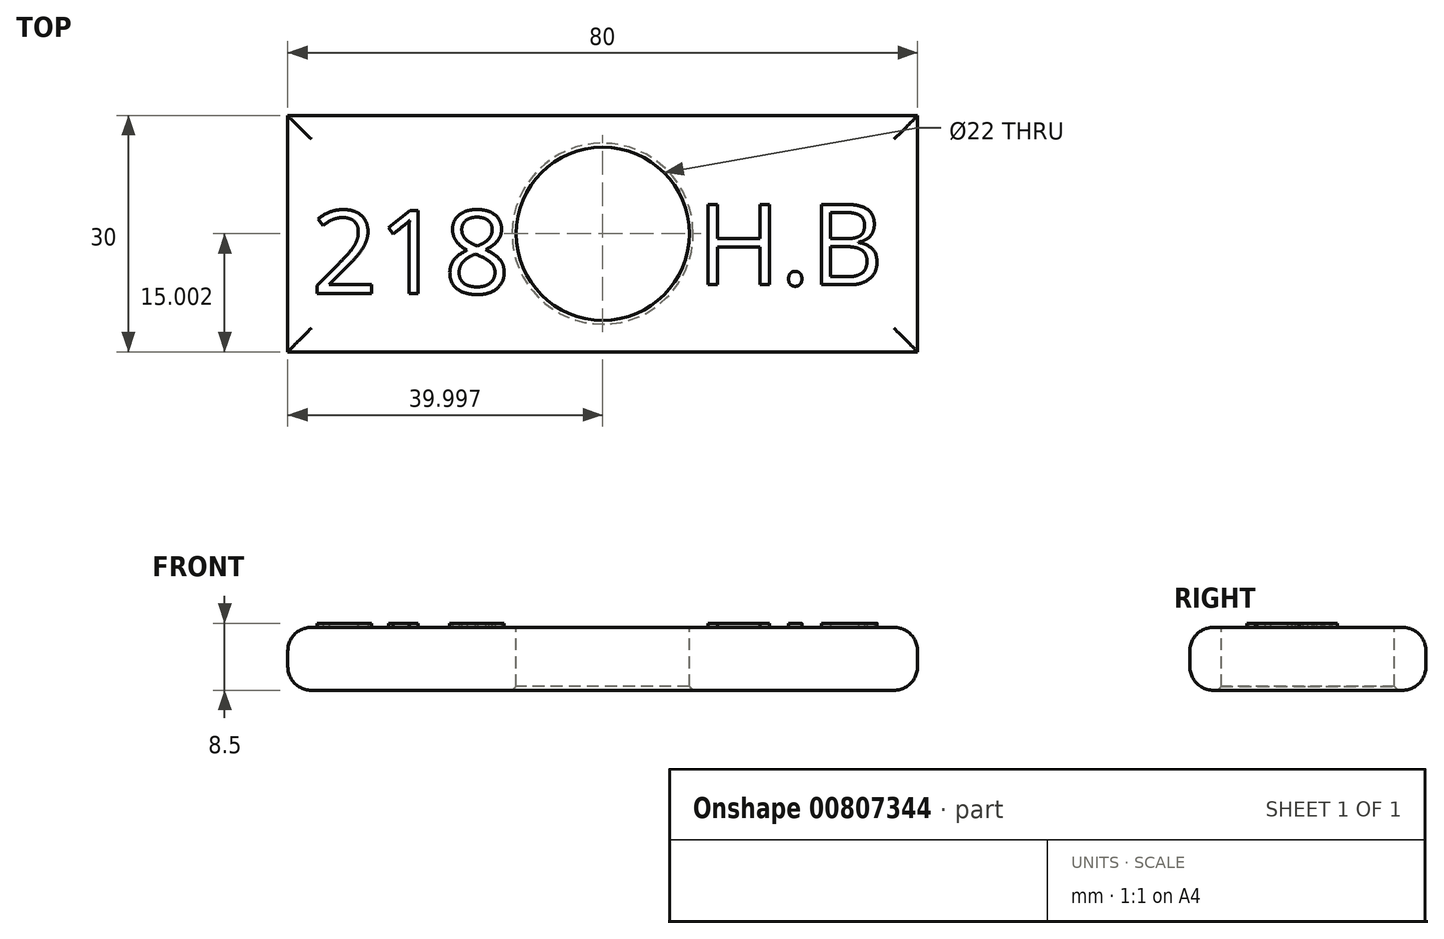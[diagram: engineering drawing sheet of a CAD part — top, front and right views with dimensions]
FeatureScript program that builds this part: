
annotation { "Feature Type Name" : "Feature", "Feature Type Description" : "" }
export const myFeature = defineFeature(function(context is Context, id is Id, definition is map)
    precondition{}
    {
        {
            var Q0;
            Q0=qCreatedBy(makeId("Top.planeOp"),FACE);
            var sketch = newSketch(context, id + "F0", { "sketchPlane" : qUnion([Q0])});
            skLineSegment(sketch, "E0.bottom", {"start": v(-37.23, 2.15) * mm, "end": v(42.77, 2.15) * mm});
            skLineSegment(sketch, "E0.top", {"start": v(-37.23, -27.85) * mm, "end": v(42.77, -27.85) * mm});
            skLineSegment(sketch, "E0.left", {"start": v(-37.23, 2.15) * mm, "end": v(-37.23, -27.85) * mm});
            skLineSegment(sketch, "E0.right", {"start": v(42.77, 2.15) * mm, "end": v(42.77, -27.85) * mm});
            skSolve(sketch);
        }
        {
            var Q0;
            Q0=makeQuery(id+"F0.imprint","IMPRINT",FACE,{"disambiguationData":[TD([[makeQuery(id+"F0.imprint","IMPRINT",EDGE,{"derivedFrom":sQuery(id+"F0.wireOp",EDGE,"E0.bottom")}),-1.0]])]});
            extrude(context, id + "F1", {"entities" : qUnion([Q0]), "depth" : 8 * mm, "offsetDistance" : 25 * mm});
        }
        {
            var Q0;
            Q0=makeQuery(id+"F1.opExtrude","CAP_FACE",FACE,{"disambiguationData":[OSD([sQuery(id+"F0.wireOp",EDGE,"E0.bottom"),sQuery(id+"F0.wireOp",EDGE,"E0.top"),sQuery(id+"F0.wireOp",EDGE,"E0.left"),sQuery(id+"F0.wireOp",EDGE,"E0.right")])],"isStart":false});
            var sketch = newSketch(context, id + "F2", { "sketchPlane" : qUnion([Q0])});
            skCircle(sketch, "E1", {"center": v(2.77, -12.85) * mm, "radius": 11 * mm});
            skPoint(sketch, "E1.centerSnap0", {"position": v(-37.23, -12.85) * mm});
            skPoint(sketch, "E1.centerSnap1", {"position": v(2.77, -27.85) * mm});
            skSolve(sketch);
        }
        {
            var Q0;
            Q0=makeQuery(id+"F2.imprint","IMPRINT",FACE,{"disambiguationData":[TD([[makeQuery(id+"F2.imprint","IMPRINT",EDGE,{"derivedFrom":sQuery(id+"F2.wireOp",EDGE,"E1")}),1.0]])]});
            extrude(context, id + "F3", {"entities" : qUnion([Q0]), "operationType" : NewBodyOperationType.REMOVE, "endBound" : BoundingType.THROUGH_ALL, "oppositeDirection" : true, "depth" : 25 * mm, "offsetDistance" : 25 * mm});
        }
        {
            var Q0;
            Q0=makeQuery(id+"F1.opExtrude","CAP_EDGE",EDGE,{"disambiguationData":[OSD([sQuery(id+"F0.wireOp",EDGE,"E0.top")])],"isStart":false});
            var Q1;
            Q1=makeQuery(id+"F1.opExtrude","CAP_EDGE",EDGE,{"disambiguationData":[OSD([sQuery(id+"F0.wireOp",EDGE,"E0.left")])],"isStart":false});
            var Q2;
            Q2=makeQuery(id+"F1.opExtrude","CAP_EDGE",EDGE,{"disambiguationData":[OSD([sQuery(id+"F0.wireOp",EDGE,"E0.bottom")])],"isStart":false});
            var Q3;
            Q3=makeQuery(id+"F1.opExtrude","CAP_EDGE",EDGE,{"disambiguationData":[OSD([sQuery(id+"F0.wireOp",EDGE,"E0.right")])],"isStart":false});
            var Q4;
            Q4=makeQuery(id+"F1.opExtrude","CAP_EDGE",EDGE,{"disambiguationData":[OSD([sQuery(id+"F0.wireOp",EDGE,"E0.right")])],"isStart":true});
            var Q5;
            Q5=makeQuery(id+"F1.opExtrude","CAP_EDGE",EDGE,{"disambiguationData":[OSD([sQuery(id+"F0.wireOp",EDGE,"E0.top")])],"isStart":true});
            var Q6;
            Q6=makeQuery(id+"F1.opExtrude","CAP_EDGE",EDGE,{"disambiguationData":[OSD([sQuery(id+"F0.wireOp",EDGE,"E0.left")])],"isStart":true});
            var Q7;
            Q7=makeQuery(id+"F1.opExtrude","CAP_EDGE",EDGE,{"disambiguationData":[OSD([sQuery(id+"F0.wireOp",EDGE,"E0.bottom")])],"isStart":true});
            fillet(context, id + "F4", {"entities" : qUnion([Q0, Q1, Q2, Q3, Q4, Q5, Q6, Q7]), "radius" : 3 * mm, "tangentPropagation" : true, "allowEdgeOverflow" : false});
        }
        {
            var Q0;
            Q0=makeQuery(id+"F1.opExtrude","CAP_FACE",FACE,{"disambiguationData":[OSD([sQuery(id+"F0.wireOp",EDGE,"E0.bottom"),sQuery(id+"F0.wireOp",EDGE,"E0.top"),sQuery(id+"F0.wireOp",EDGE,"E0.left"),sQuery(id+"F0.wireOp",EDGE,"E0.right")])],"isStart":false});
            var sketch = newSketch(context, id + "F5", { "sketchPlane" : qUnion([Q0])});
            skText(sketch, "E2", { "text": "218", "fontName": "OpenSans-Regular.ttf"});
            const initialGuessF5  = {"E2": [-0.03423, -0.02044, 1, 0, 0.0106]};
            skSetInitialGuess(sketch, initialGuessF5);
            skSolve(sketch);
        }
        {
            var Q0;
            Q0 = qSketchRegion(id + "F5", true);
            extrude(context, id + "F6", {"entities" : qUnion([Q0]), "operationType" : NewBodyOperationType.ADD, "depth" : 0.5 * mm, "offsetDistance" : 25 * mm});
        }
        {
            var Q0;
            {var subQ0=sQuery(id+"F0.wireOp",EDGE,"E0.right");var subQ1=sQuery(id+"F0.wireOp",EDGE,"E0.bottom");var subQ2=sQuery(id+"F0.wireOp",EDGE,"E0.top");var subQ3=sQuery(id+"F0.wireOp",EDGE,"E0.left");Q0=makeQuery(id+"F6.boolean.opBoolean","SPLIT",FACE,{"disambiguationData":[TD([makeQuery(id+"F3.boolean.opBoolean","COPY",FACE,{"derivedFrom":makeQuery(id+"F3.opExtrude","SWEPT_FACE",FACE,{"disambiguationData":[OSD([sQuery(id+"F2.wireOp",EDGE,"E1")])]})})])],"derivedFrom":makeQuery(id+"F1.opExtrude","CAP_FACE",FACE,{"disambiguationData":[OSD([subQ1,subQ2,subQ3,subQ0])],"isStart":false})});}
            var sketch = newSketch(context, id + "F7", { "sketchPlane" : qUnion([Q0])});
            skText(sketch, "E3", { "text": "H.B", "fontName": "OpenSans-Regular.ttf"});
            const initialGuessF7  = {"E3": [0.01477, -0.01933, 1, 0, 0.0103]};
            skSetInitialGuess(sketch, initialGuessF7);
            skSolve(sketch);
        }
        {
            var Q0;
            Q0 = qSketchRegion(id + "F7", true);
            extrude(context, id + "F8", {"entities" : qUnion([Q0]), "operationType" : NewBodyOperationType.ADD, "depth" : 0.5 * mm, "offsetDistance" : 25 * mm});
        }
        {
            var Q0;
            Q0=makeQuery(id+"F3.boolean.opBoolean","COPY",EDGE,{"derivedFrom":makeQuery(id+"F3.opExtrude","CAP_EDGE",EDGE,{"disambiguationData":[OSD([sQuery(id+"F2.wireOp",EDGE,"E1")])],"isStart":true})});
            var Q1;
            Q1=makeQuery(id+"F3.boolean.opBoolean","INTERSECT",EDGE,{"derivedFrom":[makeQuery(id+"F1.opExtrude","CAP_FACE",FACE,{"disambiguationData":[OSD([sQuery(id+"F0.wireOp",EDGE,"E0.bottom"),sQuery(id+"F0.wireOp",EDGE,"E0.top"),sQuery(id+"F0.wireOp",EDGE,"E0.left"),sQuery(id+"F0.wireOp",EDGE,"E0.right")])],"isStart":true}),makeQuery(id+"F3.opExtrude","SWEPT_FACE",FACE,{"disambiguationData":[OSD([sQuery(id+"F2.wireOp",EDGE,"E1")])]})]});
            chamfer(context, id + "F9", {"entities" : qUnion([Q0, Q1]), "width" : 0.5 * mm, "tangentPropagation" : true});
        }
    });
